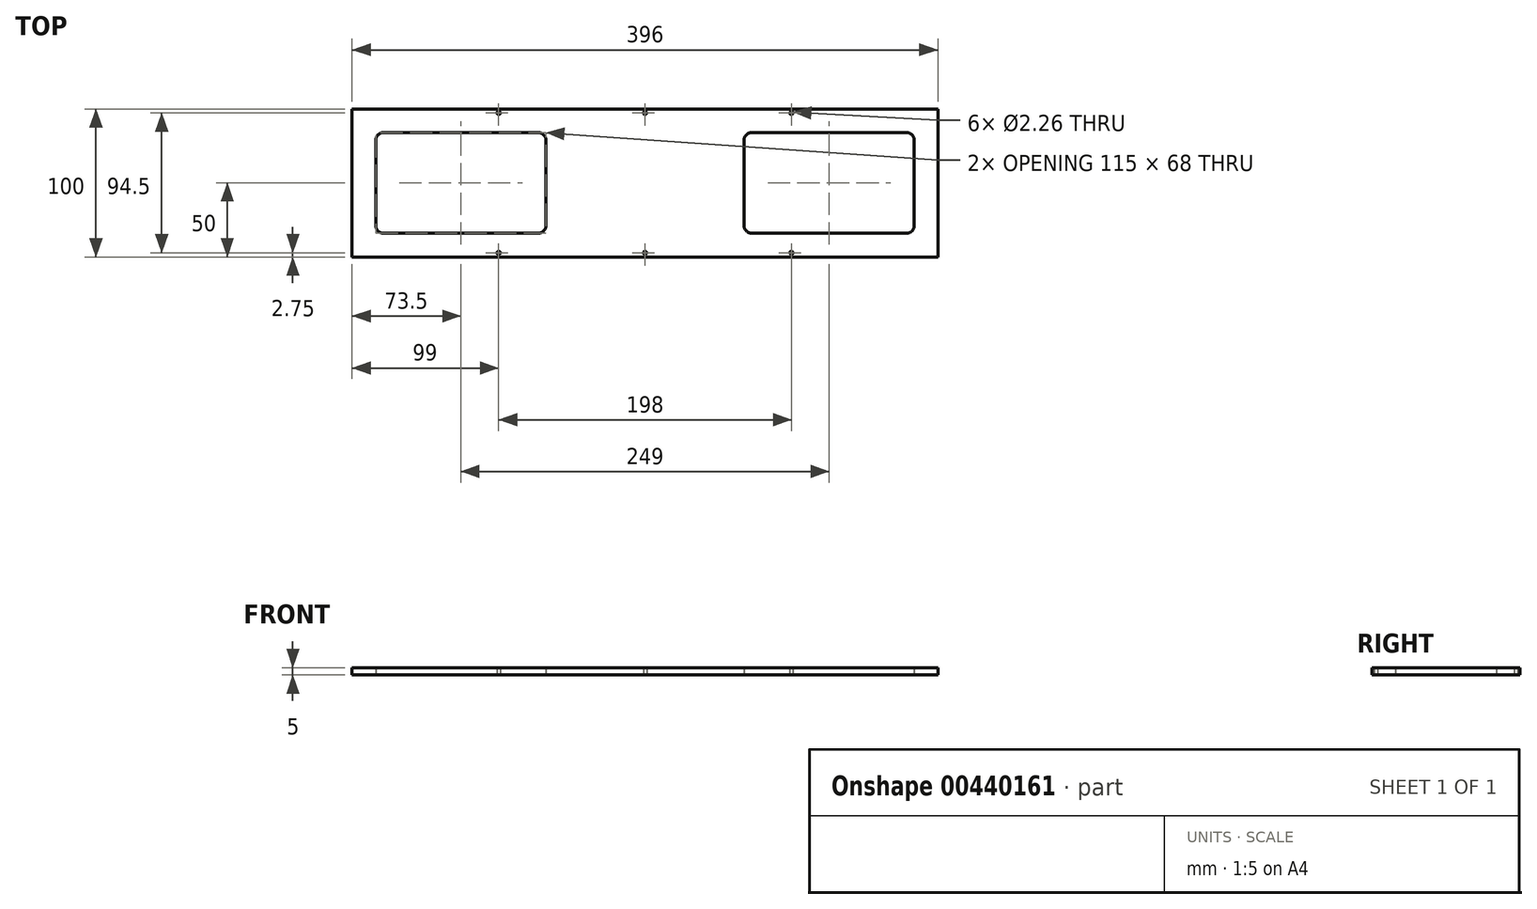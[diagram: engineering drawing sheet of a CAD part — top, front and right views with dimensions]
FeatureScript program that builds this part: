
annotation { "Feature Type Name" : "Feature", "Feature Type Description" : "" }
export const myFeature = defineFeature(function(context is Context, id is Id, definition is map)
    precondition{}
    {
        {
            var Q0;
            Q0=qCreatedBy(makeId("Top.planeOp"),FACE);
            var sketch = newSketch(context, id + "F0", { "sketchPlane" : qUnion([Q0])});
            skLineSegment(sketch, "E0.bottom", {"start": v(-198, 50) * mm, "end": v(198, 50) * mm});
            skLineSegment(sketch, "E0.top", {"start": v(-198, -50) * mm, "end": v(198, -50) * mm});
            skLineSegment(sketch, "E0.left", {"start": v(-198, 50) * mm, "end": v(-198, -50) * mm});
            skLineSegment(sketch, "E0.right", {"start": v(198, 50) * mm, "end": v(198, -50) * mm});
            skPoint(sketch, "E1", {"position": v(-198, 0) * mm});
            skPoint(sketch, "E2", {"position": v(0, 50) * mm});
            skLineSegment(sketch, "E3.bottom", {"start": v(-177, 34) * mm, "end": v(-72, 34) * mm});
            skLineSegment(sketch, "E3.top", {"start": v(-177, -34) * mm, "end": v(-72, -34) * mm});
            skLineSegment(sketch, "E3.left", {"start": v(-182, 29) * mm, "end": v(-182, -29) * mm});
            skLineSegment(sketch, "E3.right", {"start": v(-67, 29) * mm, "end": v(-67, -29) * mm});
            skLineSegment(sketch, "E4.bottom", {"start": v(72, 34) * mm, "end": v(177, 34) * mm});
            skLineSegment(sketch, "E4.top", {"start": v(72, -34) * mm, "end": v(177, -34) * mm});
            skLineSegment(sketch, "E4.left", {"start": v(67, 29) * mm, "end": v(67, -29) * mm});
            skLineSegment(sketch, "E4.right", {"start": v(182, 29) * mm, "end": v(182, -29) * mm});
            skPoint(sketch, "E5", {"position": v(-182, 0) * mm});
            skPoint(sketch, "E6.visualSharp", {"position": v(-182, 34) * mm});
            skArc(sketch, "E6.filletArc", {"start": v(-177, 34) * mm, "mid": v(-180.54, 32.54) * mm, "end": v(-182, 29) * mm});
            skPoint(sketch, "E7.visualSharp", {"position": v(-67, 34) * mm});
            skArc(sketch, "E7.filletArc", {"start": v(-67, 29) * mm, "mid": v(-68.46, 32.54) * mm, "end": v(-72, 34) * mm});
            skPoint(sketch, "E8.visualSharp", {"position": v(-67, -34) * mm});
            skArc(sketch, "E8.filletArc", {"start": v(-72, -34) * mm, "mid": v(-68.46, -32.54) * mm, "end": v(-67, -29) * mm});
            skPoint(sketch, "E9.visualSharp", {"position": v(-182, -34) * mm});
            skArc(sketch, "E9.filletArc", {"start": v(-182, -29) * mm, "mid": v(-180.54, -32.54) * mm, "end": v(-177, -34) * mm});
            skPoint(sketch, "E10.visualSharp", {"position": v(67, 34) * mm});
            skArc(sketch, "E10.filletArc", {"start": v(72, 34) * mm, "mid": v(68.46, 32.54) * mm, "end": v(67, 29) * mm});
            skPoint(sketch, "E11.visualSharp", {"position": v(67, -34) * mm});
            skArc(sketch, "E11.filletArc", {"start": v(67, -29) * mm, "mid": v(68.46, -32.54) * mm, "end": v(72, -34) * mm});
            skPoint(sketch, "E12.visualSharp", {"position": v(182, 34) * mm});
            skArc(sketch, "E12.filletArc", {"start": v(182, 29) * mm, "mid": v(180.54, 32.54) * mm, "end": v(177, 34) * mm});
            skPoint(sketch, "E13.visualSharp", {"position": v(182, -34) * mm});
            skArc(sketch, "E13.filletArc", {"start": v(177, -34) * mm, "mid": v(180.54, -32.54) * mm, "end": v(182, -29) * mm});
            skCircle(sketch, "E14", {"center": v(-99, 47.25) * mm, "radius": 1.13 * mm});
            skCircle(sketch, "E15", {"center": v(-99, -47.25) * mm, "radius": 1.13 * mm});
            skCircle(sketch, "E16", {"center": v(0, 47.25) * mm, "radius": 1.13 * mm});
            skCircle(sketch, "E17", {"center": v(0, -47.25) * mm, "radius": 1.13 * mm});
            skCircle(sketch, "E18", {"center": v(99, 47.25) * mm, "radius": 1.13 * mm});
            skCircle(sketch, "E19", {"center": v(99, -47.25) * mm, "radius": 1.13 * mm});
            skSolve(sketch);
        }
        {
            var Q0;
            Q0 = qSketchRegion(id + "F0", true);
            extrude(context, id + "F1", {"entities" : qUnion([Q0]), "depth" : 5 * mm});
        }
    });
